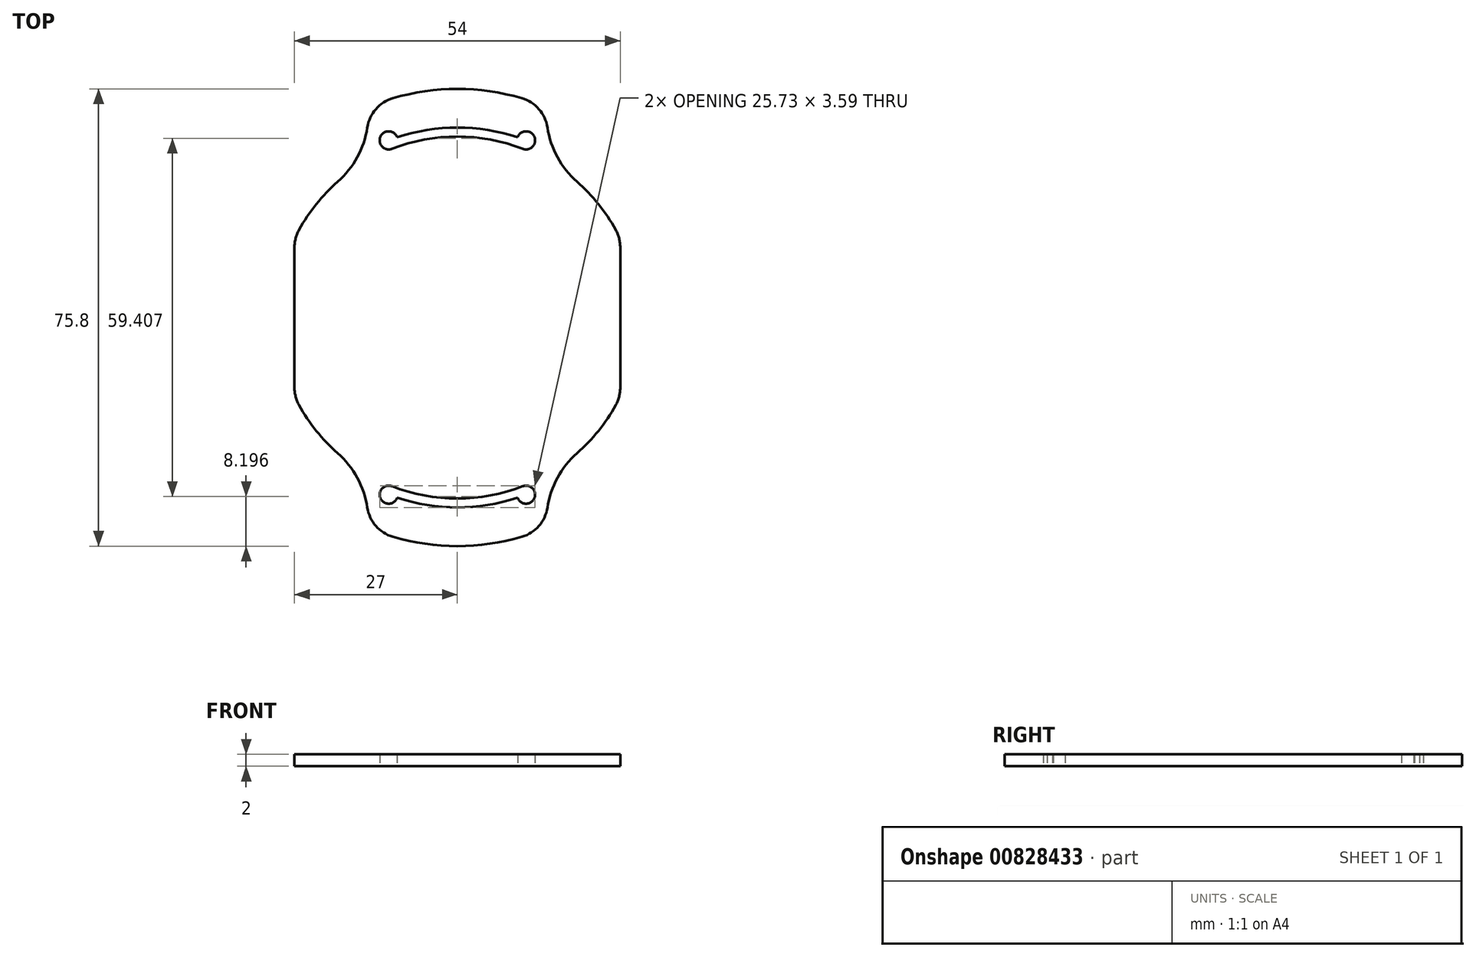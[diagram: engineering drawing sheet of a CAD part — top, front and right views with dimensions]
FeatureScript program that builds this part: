
annotation { "Feature Type Name" : "Feature", "Feature Type Description" : "" }
export const myFeature = defineFeature(function(context is Context, id is Id, definition is map)
    precondition{}
    {
        {
            var Q0;
            Q0=qCreatedBy(makeId("Top.planeOp"),FACE);
            var sketch = newSketch(context, id + "F0", { "sketchPlane" : qUnion([Q0])});
            skCircle(sketch, "E0", {"center": v(0, 0) * mm, "radius": 22.37 * mm, "construction": true});
            skCircle(sketch, "E1", {"center": v(0, 0) * mm, "radius": 25 * mm, "construction": true});
            skLineSegment(sketch, "E2", {"start": v(0, 73.38) * mm, "end": v(0, -74.08) * mm, "construction": true});
            skLineSegment(sketch, "E3.0", {"start": v(-15, 73.38) * mm, "end": v(-15, -74.08) * mm, "construction": true});
            skLineSegment(sketch, "E4.0", {"start": v(15, 73.38) * mm, "end": v(15, -74.08) * mm, "construction": true});
            skCircle(sketch, "E5", {"center": v(0, 0) * mm, "radius": 37.9 * mm});
            skCircle(sketch, "E6", {"center": v(0, 0) * mm, "radius": 30 * mm});
            skCircle(sketch, "E7", {"center": v(0, 0) * mm, "radius": 31.5 * mm});
            skCircle(sketch, "E8", {"center": v(-11.39, 29.37) * mm, "radius": 1.5 * mm});
            skCircle(sketch, "E9.MirrorC", {"center": v(11.39, 29.37) * mm, "radius": 1.5 * mm});
            skLineSegment(sketch, "E10", {"start": v(-15, 34.8) * mm, "end": v(-15, 20) * mm});
            skLineSegment(sketch, "E11", {"start": v(15, 34.8) * mm, "end": v(15, 20) * mm});
            skArc(sketch, "E12", {"start": v(-15, 20) * mm, "mid": v(-22.36, 11.18) * mm, "end": v(-25, 0) * mm});
            skArc(sketch, "E13", {"start": v(15, 20) * mm, "mid": v(22.36, 11.18) * mm, "end": v(25, 0) * mm});
            skCircle(sketch, "E14.MirrorC", {"center": v(-11.39, -29.37) * mm, "radius": 1.5 * mm});
            skCircle(sketch, "E15.MirrorC", {"center": v(11.39, -29.37) * mm, "radius": 1.5 * mm});
            skArc(sketch, "E16.MirrorCS", {"start": v(-15, -20) * mm, "mid": v(-22.36, -11.18) * mm, "end": v(-25, 0) * mm});
            skArc(sketch, "E17.MirrorCS", {"start": v(15, -20) * mm, "mid": v(22.36, -11.18) * mm, "end": v(25, 0) * mm});
            skLineSegment(sketch, "E18", {"start": v(-15, -25.98) * mm, "end": v(-15, -34.8) * mm});
            skLineSegment(sketch, "E19", {"start": v(15, -25.98) * mm, "end": v(15, -34.8) * mm});
            skLineSegment(sketch, "E20.0", {"start": v(27, 73.38) * mm, "end": v(27, -74.08) * mm});
            skLineSegment(sketch, "E21.0", {"start": v(-27, 73.38) * mm, "end": v(-27, -74.08) * mm});
            skSolve(sketch);
        }
        {
            var Q0;
            {var subQ3=sQuery(id+"F0.wireOp",EDGE,"E10");var subQ11=sQuery(id+"F0.wireOp",EDGE,"E5");var subQ12=makeQuery(id+"F0.imprint","INTERSECT",VERTEX,{"derivedFrom":[subQ11,subQ3]});Q0=makeQuery(id+"F0.imprint","IMPRINT",FACE,{"disambiguationData":[TD([[makeQuery(id+"F0.imprint","IMPRINT",EDGE,{"disambiguationData":[TD([[subQ12,1.0]])],"derivedFrom":subQ11}),1.0]])]});}
            var Q1;
            {var subQ0=sQuery(id+"F0.wireOp",EDGE,"E10");var subQ1=sQuery(id+"F0.wireOp",EDGE,"E6");var subQ2=makeQuery(id+"F0.imprint","INTERSECT",VERTEX,{"derivedFrom":[subQ1,subQ0]});Q1=makeQuery(id+"F0.imprint","IMPRINT",FACE,{"disambiguationData":[TD([[makeQuery(id+"F0.imprint","IMPRINT",EDGE,{"disambiguationData":[TD([[subQ2,1.0]])],"derivedFrom":subQ1}),-1.0]])]});}
            var Q2;
            {var subQ0=sQuery(id+"F0.wireOp",EDGE,"E11");var subQ1=sQuery(id+"F0.wireOp",EDGE,"E6");var subQ2=makeQuery(id+"F0.imprint","INTERSECT",VERTEX,{"derivedFrom":[subQ1,subQ0]});Q2=makeQuery(id+"F0.imprint","IMPRINT",FACE,{"disambiguationData":[TD([[makeQuery(id+"F0.imprint","IMPRINT",EDGE,{"disambiguationData":[TD([[subQ2,-1.0]])],"derivedFrom":subQ1}),-1.0]])]});}
            var Q3;
            {var subQ5=sQuery(id+"F0.wireOp",EDGE,"E18");var subQ6=sQuery(id+"F0.wireOp",EDGE,"E5");var subQ7=makeQuery(id+"F0.imprint","INTERSECT",VERTEX,{"derivedFrom":[subQ6,subQ5]});Q3=makeQuery(id+"F0.imprint","IMPRINT",FACE,{"disambiguationData":[TD([[makeQuery(id+"F0.imprint","IMPRINT",EDGE,{"disambiguationData":[TD([[subQ7,-1.0]])],"derivedFrom":subQ6}),1.0]])]});}
            var Q4;
            {var subQ0=sQuery(id+"F0.wireOp",EDGE,"E18");var subQ1=sQuery(id+"F0.wireOp",EDGE,"E6");var subQ2=makeQuery(id+"F0.imprint","INTERSECT",VERTEX,{"derivedFrom":[subQ1,subQ0]});Q4=makeQuery(id+"F0.imprint","IMPRINT",FACE,{"disambiguationData":[TD([[makeQuery(id+"F0.imprint","IMPRINT",EDGE,{"disambiguationData":[TD([[subQ2,-1.0]])],"derivedFrom":subQ1}),-1.0]])]});}
            var Q5;
            {var subQ0=sQuery(id+"F0.wireOp",EDGE,"E19");var subQ1=sQuery(id+"F0.wireOp",EDGE,"E6");var subQ2=makeQuery(id+"F0.imprint","INTERSECT",VERTEX,{"derivedFrom":[subQ1,subQ0]});Q5=makeQuery(id+"F0.imprint","IMPRINT",FACE,{"disambiguationData":[TD([[makeQuery(id+"F0.imprint","IMPRINT",EDGE,{"disambiguationData":[TD([[subQ2,1.0]])],"derivedFrom":subQ1}),-1.0]])]});}
            var Q6;
            {var subQ0=sQuery(id+"F0.wireOp",EDGE,"E6");var subQ12=makeQuery(id+"F0.imprint","INTERSECT",VERTEX,{"derivedFrom":[subQ0,sQuery(id+"F0.wireOp",EDGE,"E11")]});Q6=makeQuery(id+"F0.imprint","IMPRINT",FACE,{"disambiguationData":[TD([[makeQuery(id+"F0.imprint","IMPRINT",EDGE,{"disambiguationData":[TD([[subQ12,1.0]])],"derivedFrom":subQ0}),1.0]])]});}
            extrude(context, id + "F1", {"entities" : qUnion([Q0, Q1, Q2, Q3, Q4, Q5, Q6]), "depth" : 2 * mm, "offsetDistance" : 25 * mm});
        }
        {
            var Q0;
            Q0=makeQuery(id+"F1.opExtrude","SWEPT_EDGE",EDGE,{"disambiguationData":[OSD([sQuery(id+"F0.wireOp",EDGE,"E5"),sQuery(id+"F0.wireOp",EDGE,"E18")])]});
            var Q1;
            Q1=makeQuery(id+"F1.opExtrude","SWEPT_EDGE",EDGE,{"disambiguationData":[OSD([sQuery(id+"F0.wireOp",EDGE,"E5"),sQuery(id+"F0.wireOp",EDGE,"E19")])]});
            var Q2;
            Q2=makeQuery(id+"F1.opExtrude","SWEPT_EDGE",EDGE,{"disambiguationData":[OSD([sQuery(id+"F0.wireOp",EDGE,"E5"),sQuery(id+"F0.wireOp",EDGE,"E11")])]});
            var Q3;
            Q3=makeQuery(id+"F1.opExtrude","SWEPT_EDGE",EDGE,{"disambiguationData":[OSD([sQuery(id+"F0.wireOp",EDGE,"E5"),sQuery(id+"F0.wireOp",EDGE,"E10")])]});
            var Q4;
            {var subQ0=sQuery(id+"F0.wireOp",EDGE,"E20.0");var subQ1=sQuery(id+"F0.wireOp",EDGE,"E6");Q4=makeQuery(id+"F1.opExtrude","SWEPT_EDGE",EDGE,{"disambiguationData":[OSD([subQ1,subQ0]),TDD([makeQuery(id+"F0.imprint","INTERSECT",VERTEX,{"disambiguationData":[OD(0.0)],"derivedFrom":[subQ1,subQ0]})])]});}
            var Q5;
            {var subQ0=sQuery(id+"F0.wireOp",EDGE,"E20.0");var subQ1=sQuery(id+"F0.wireOp",EDGE,"E6");Q5=makeQuery(id+"F1.opExtrude","SWEPT_EDGE",EDGE,{"disambiguationData":[OSD([subQ1,subQ0]),TDD([makeQuery(id+"F0.imprint","INTERSECT",VERTEX,{"disambiguationData":[OD(1.0)],"derivedFrom":[subQ1,subQ0]})])]});}
            var Q6;
            {var subQ0=sQuery(id+"F0.wireOp",EDGE,"E21.0");var subQ1=sQuery(id+"F0.wireOp",EDGE,"E6");Q6=makeQuery(id+"F1.opExtrude","SWEPT_EDGE",EDGE,{"disambiguationData":[OSD([subQ1,subQ0]),TDD([makeQuery(id+"F0.imprint","INTERSECT",VERTEX,{"disambiguationData":[OD(0.0)],"derivedFrom":[subQ1,subQ0]})])]});}
            var Q7;
            {var subQ0=sQuery(id+"F0.wireOp",EDGE,"E21.0");var subQ1=sQuery(id+"F0.wireOp",EDGE,"E6");Q7=makeQuery(id+"F1.opExtrude","SWEPT_EDGE",EDGE,{"disambiguationData":[OSD([subQ1,subQ0]),TDD([makeQuery(id+"F0.imprint","INTERSECT",VERTEX,{"disambiguationData":[OD(1.0)],"derivedFrom":[subQ1,subQ0]})])]});}
            fillet(context, id + "F2", {"entities" : qUnion([Q0, Q1, Q2, Q3, Q4, Q5, Q6, Q7]), "tangentPropagation" : true, "radius" : 6 * mm, "defaultsChanged" : false, "vertexSettings" : [], "allowEdgeOverflow" : false});
        }
        {
            var Q0;
            Q0=makeQuery(id+"F1.opExtrude","SWEPT_EDGE",EDGE,{"disambiguationData":[OSD([sQuery(id+"F0.wireOp",EDGE,"E6"),sQuery(id+"F0.wireOp",EDGE,"E18")])]});
            var Q1;
            Q1=makeQuery(id+"F1.opExtrude","SWEPT_EDGE",EDGE,{"disambiguationData":[OSD([sQuery(id+"F0.wireOp",EDGE,"E6"),sQuery(id+"F0.wireOp",EDGE,"E19")])]});
            var Q2;
            Q2=makeQuery(id+"F1.opExtrude","SWEPT_EDGE",EDGE,{"disambiguationData":[OSD([sQuery(id+"F0.wireOp",EDGE,"E6"),sQuery(id+"F0.wireOp",EDGE,"E11")])]});
            var Q3;
            Q3=makeQuery(id+"F1.opExtrude","SWEPT_EDGE",EDGE,{"disambiguationData":[OSD([sQuery(id+"F0.wireOp",EDGE,"E6"),sQuery(id+"F0.wireOp",EDGE,"E10")])]});
            fillet(context, id + "F3", {"entities" : qUnion([Q0, Q1, Q2, Q3]), "tangentPropagation" : true, "radius" : 15 * mm, "defaultsChanged" : false, "vertexSettings" : [], "allowEdgeOverflow" : false});
        }
    });
